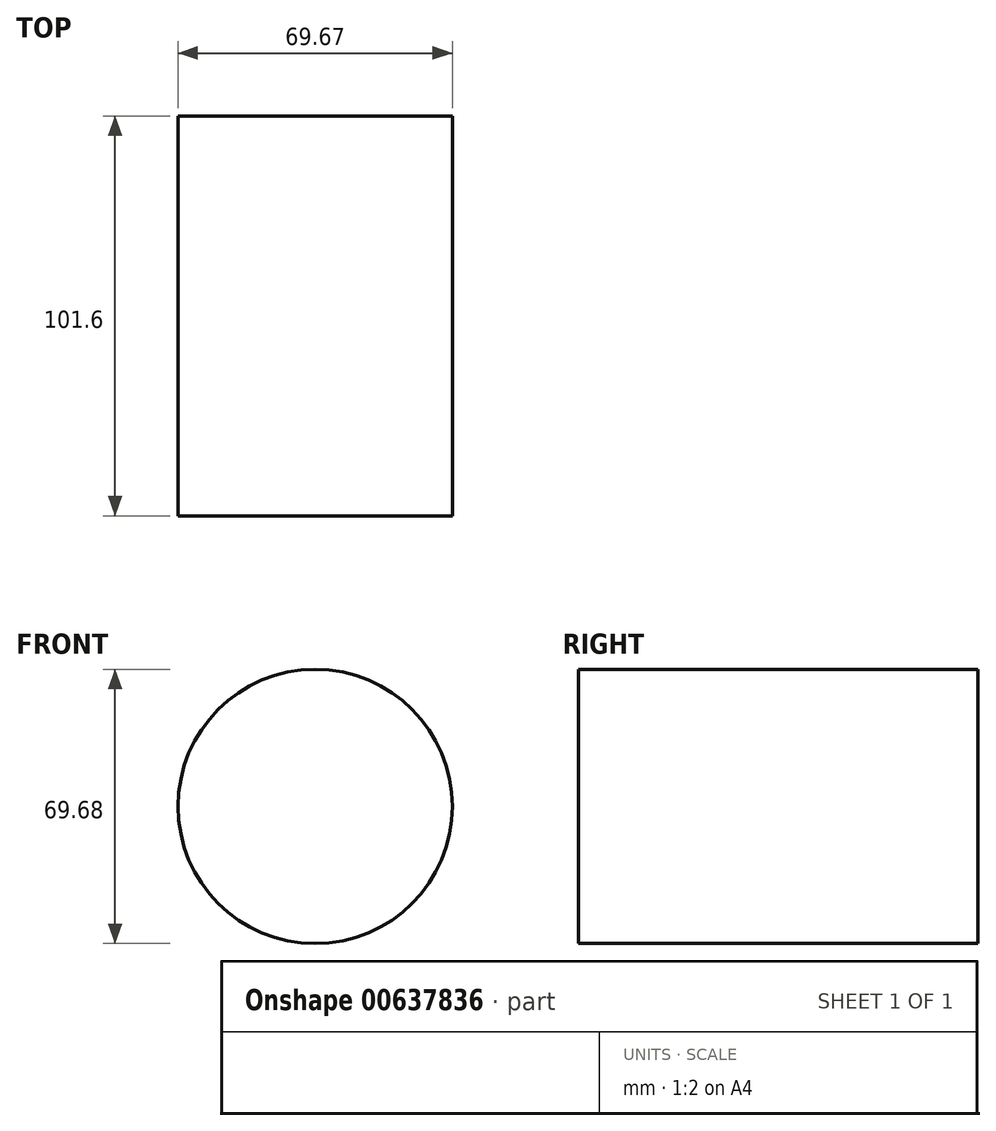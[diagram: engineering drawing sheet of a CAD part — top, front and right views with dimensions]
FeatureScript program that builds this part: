
annotation { "Feature Type Name" : "Feature", "Feature Type Description" : "" }
export const myFeature = defineFeature(function(context is Context, id is Id, definition is map)
    precondition{}
    {
        {
            var Q0;
            Q0=qCreatedBy(makeId("Front.planeOp"),FACE);
            var sketch = newSketch(context, id + "F0", { "sketchPlane" : qUnion([Q0])});
            skCircle(sketch, "E0", {"center": v(-48.4, 34.66) * mm, "radius": 34.84 * mm});
            skSolve(sketch);
        }
        {
            var Q0;
            Q0=makeQuery(id+"F0.imprint","IMPRINT",FACE,{"disambiguationData":[TD([[makeQuery(id+"F0.imprint","IMPRINT",EDGE,{"derivedFrom":sQuery(id+"F0.wireOp",EDGE,"E0")}),1.0]])]});
            extrude(context, id + "F1", {"entities" : qUnion([Q0]), "depth" : 101.6 * mm, "offsetDistance" : 25.4 * mm});
        }
    });
